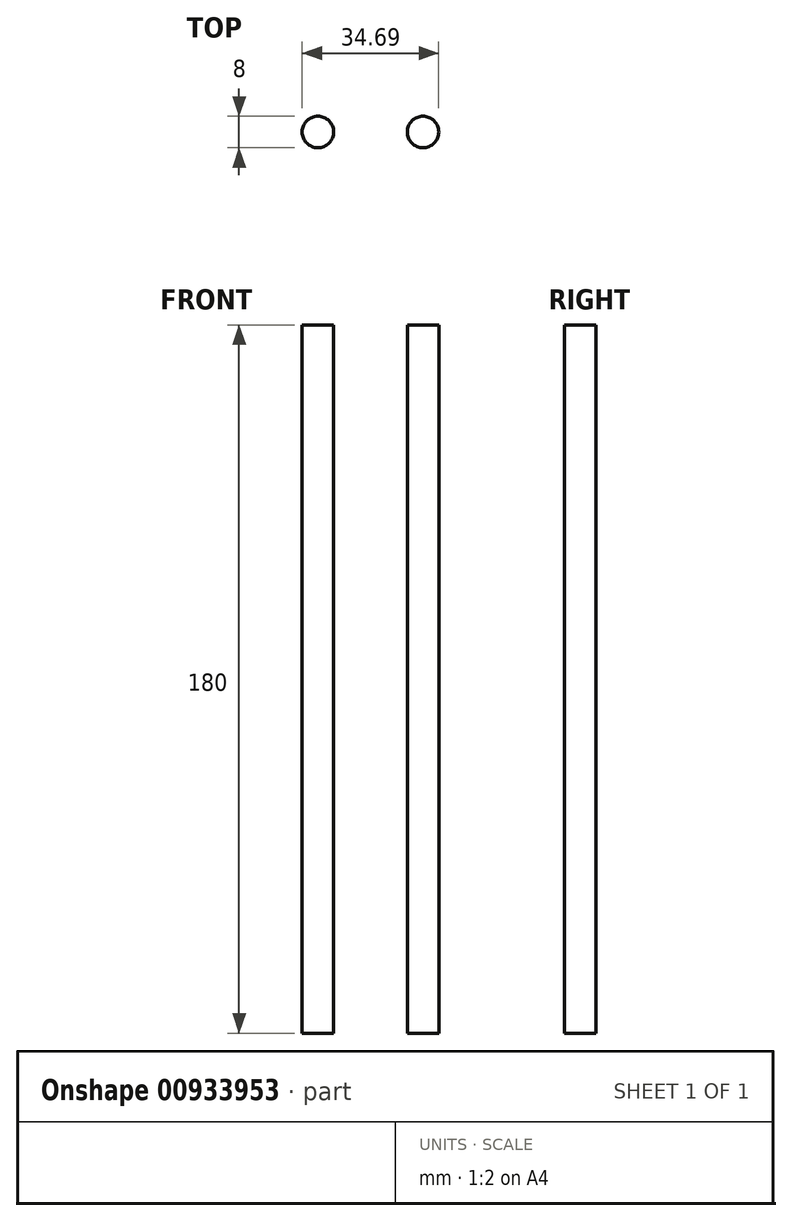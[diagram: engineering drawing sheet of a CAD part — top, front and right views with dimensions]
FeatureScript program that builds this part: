
annotation { "Feature Type Name" : "Feature", "Feature Type Description" : "" }
export const myFeature = defineFeature(function(context is Context, id is Id, definition is map)
    precondition{}
    {
        {
            var Q0;
            Q0=qCreatedBy(makeId("Top.planeOp"),FACE);
            var sketch = newSketch(context, id + "F0", { "sketchPlane" : qUnion([Q0])});
            skCircle(sketch, "E0", {"center": v(-41.58, 0) * mm, "radius": 4 * mm});
            skCircle(sketch, "E1", {"center": v(-14.89, 0) * mm, "radius": 4 * mm});
            skSolve(sketch);
        }
        {
            var Q0;
            Q0=makeQuery(id+"F0.imprint","IMPRINT",FACE,{"disambiguationData":[TD([[makeQuery(id+"F0.imprint","IMPRINT",EDGE,{"derivedFrom":sQuery(id+"F0.wireOp",EDGE,"E0")}),1.0]])]});
            var Q1;
            Q1=makeQuery(id+"F0.imprint","IMPRINT",FACE,{"disambiguationData":[TD([[makeQuery(id+"F0.imprint","IMPRINT",EDGE,{"derivedFrom":sQuery(id+"F0.wireOp",EDGE,"E1")}),1.0]])]});
            extrude(context, id + "F1", {"entities" : qUnion([Q0, Q1]), "depth" : 180 * mm, "offsetDistance" : 25 * mm});
        }
    });
